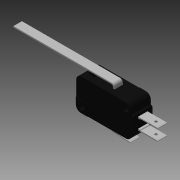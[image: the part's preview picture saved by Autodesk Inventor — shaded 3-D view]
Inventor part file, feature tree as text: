
AUTODESK INVENTOR PART (.ipt)
format: ipt  version: 2016 SP1 (Build 200210100, 210)  size: 339,456 bytes
history: native  units: in
note: dims shown in document units (in); Inventor stores cm internally (conversion verified against a paired STEP export)
features: extrude x6, sketch x2, hole x2
ambient origin geometry x8: Origin, YZ Plane, XZ Plane, XY Plane, X Axis, Y Axis, Z Axis, Center Point
bodies: Solid1 (feature_tree)
feature tree (10):
  sketch  "Sketch1"  dims[d0=0.8749in d1=0.8749in d2=1.135in d3=1.135in]
  extrude  "Extrusion1"  Depth=1.135in
  sketch  "Sketch2"  dims[d4=0.4054in d5=0.4054in d6=0.17in d7=0.0in d8=0.3854in d9=0.3854in d10=0.6024in d11=0.6024in d12=0.402in d13=0.402in d14=0.24in d15=0.24in d16=0.6529in d17=0.6529in d18=2.3471in d19=2.3471in d20=0.02in d21=0.02in d22=0.125in d23=0.125in d24=0.187in d25=0.187in d26=0.126in d27=0.126in d28=0.235in d29=0.235in d30=0.0104in d31=0.0104in d32=0.54in d33=0.54in d34=0.323in d35=0.323in d36=0.114in d37=0.114in d38=0.11in d39=0.11in d40=0.116in d41=0.116in d42=0.626in d43=0.626in d44=0.04in d45=0.04in d46=0.386in d47=0.0in d48=0.402in d49=0.0in d50=0.402in d51=0.0in d52=0.15in d53=0.0in d54=0.17in d55=0.0in d56=0.187in d57=0.0in d58=0.125in d59=0.0935in d60=0.055in d61=0.5in d62=0.375in d63=0.25in d64=0.5635in d65=0.75in d66=0.8108in d67=0.0935in d68=0.125in d69=0.055in d70=0.5in d71=0.375in d72=0.25in d73=0.5635in d74=0.75in d75=0.8108in]
  extrude  "Extrusion2"  Depth=0.17in TaperAngle=0.0deg
  extrude  "Extrusion3"  Depth=0.187in
  extrude  "Extrusion4"  Depth=0.187in
  extrude  "Extrusion5"  Depth=0.402in
  extrude  "Extrusion6"  Depth=0.24in
  hole  "Hole1"  [1 undecoded]
  hole  "Hole2"  [1 undecoded]
note: 2 required parameter values undecoded (feature->parameter linkage not recoverable at this tier; creation-order binding heuristic only, values carry confidence <= 0.55)
